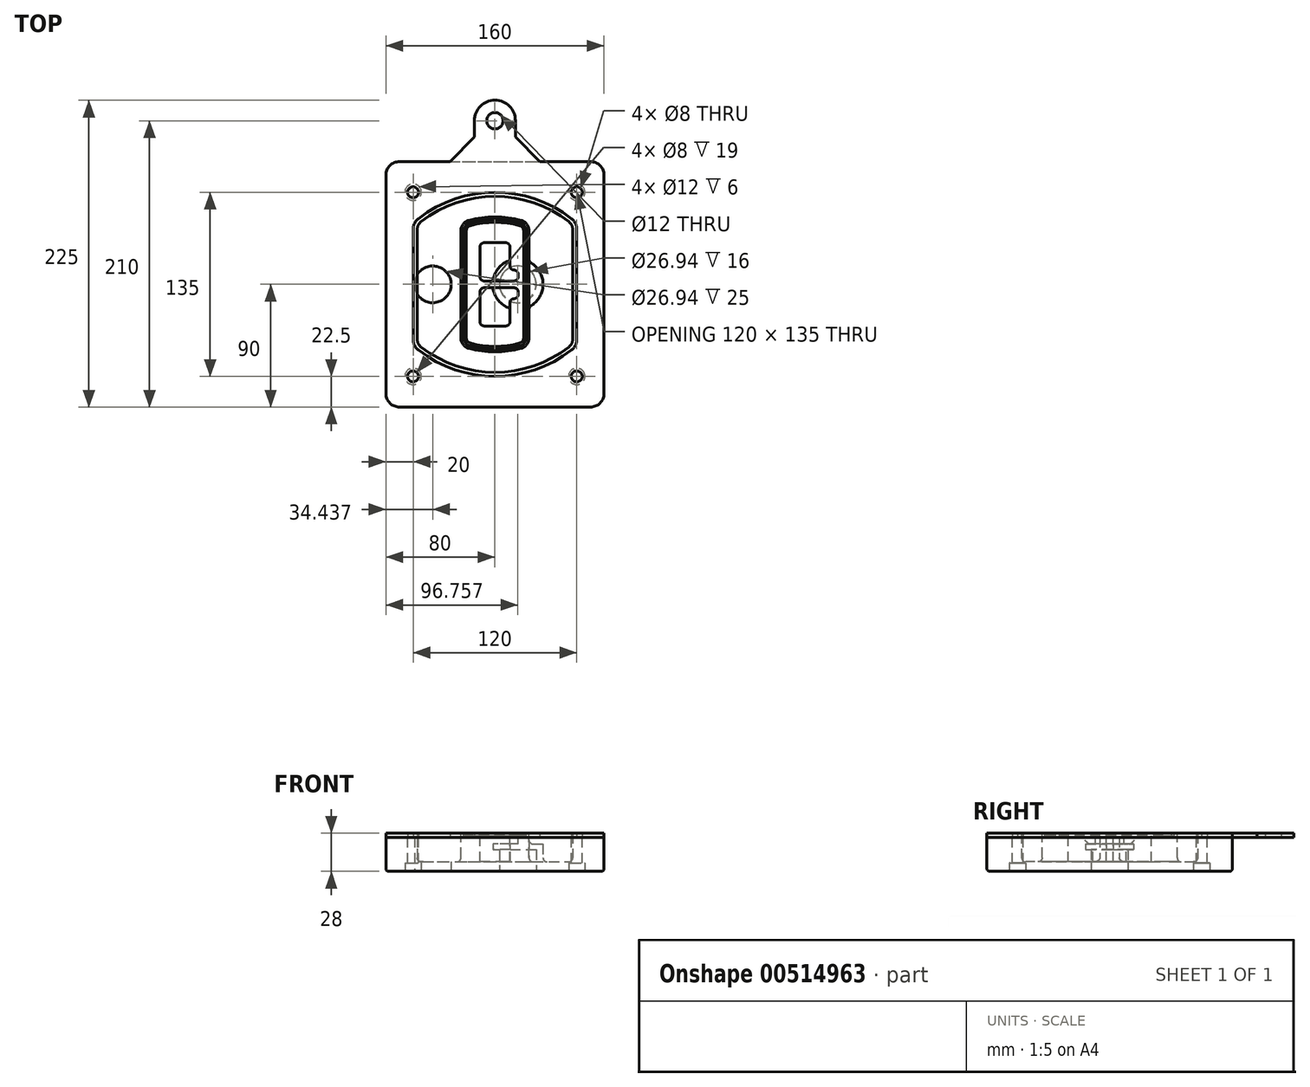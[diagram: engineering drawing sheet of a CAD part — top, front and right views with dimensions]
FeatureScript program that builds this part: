
annotation { "Feature Type Name" : "Feature", "Feature Type Description" : "" }
export const myFeature = defineFeature(function(context is Context, id is Id, definition is map)
    precondition{}
    {
        {
            var Q0;
            Q0=qCreatedBy(makeId("Top.planeOp"),FACE);
            var sketch = newSketch(context, id + "F0", { "sketchPlane" : qUnion([Q0])});
            skPoint(sketch, "E0.rect.middle", {"position": v(0, 0) * mm});
            skLineSegment(sketch, "E1.bottom", {"start": v(-70, -90) * mm, "end": v(70, -90) * mm});
            skLineSegment(sketch, "E1.top", {"start": v(-70, 90) * mm, "end": v(70, 90) * mm});
            skLineSegment(sketch, "E1.left", {"start": v(-80, -80) * mm, "end": v(-80, 80) * mm});
            skLineSegment(sketch, "E1.right", {"start": v(80, -80) * mm, "end": v(80, 80) * mm});
            skLineSegment(sketch, "E2", {"start": v(-80, 90) * mm, "end": v(80, -90) * mm, "construction": true});
            skLineSegment(sketch, "E3", {"start": v(80, 90) * mm, "end": v(-80, -90) * mm, "construction": true});
            skCircle(sketch, "E4", {"center": v(-60, 67.5) * mm, "radius": 4 * mm});
            skCircle(sketch, "E5", {"center": v(60, 67.5) * mm, "radius": 4 * mm});
            skCircle(sketch, "E6", {"center": v(60, -67.5) * mm, "radius": 4 * mm});
            skCircle(sketch, "E7", {"center": v(-60, -67.5) * mm, "radius": 4 * mm});
            skLineSegment(sketch, "E8", {"start": v(-60, 67.5) * mm, "end": v(60, 67.5) * mm, "construction": true});
            skLineSegment(sketch, "E9", {"start": v(60, 67.5) * mm, "end": v(60, -67.5) * mm, "construction": true});
            skLineSegment(sketch, "E10", {"start": v(60, -67.5) * mm, "end": v(-60, -67.5) * mm, "construction": true});
            skLineSegment(sketch, "E11", {"start": v(-60, -67.5) * mm, "end": v(-60, 67.5) * mm, "construction": true});
            skLineSegment(sketch, "E12", {"start": v(-60, 40.3) * mm, "end": v(-60, -40.3) * mm});
            skLineSegment(sketch, "E13", {"start": v(60, 40.3) * mm, "end": v(60, -40.3) * mm});
            skArc(sketch, "E14", {"start": v(56.15, 48.18) * mm, "mid": v(0, 67.5) * mm, "end": v(-56.15, 48.18) * mm});
            skArc(sketch, "E15", {"start": v(-56.15, -48.18) * mm, "mid": v(0, -67.5) * mm, "end": v(56.15, -48.18) * mm});
            skLineSegment(sketch, "E16", {"start": v(-60, 0) * mm, "end": v(60, 0) * mm, "construction": true});
            skPoint(sketch, "E17.visualSharp", {"position": v(-60, -45) * mm});
            skArc(sketch, "E17.filletArc", {"start": v(-60, -40.3) * mm, "mid": v(-58.99, -44.68) * mm, "end": v(-56.15, -48.18) * mm});
            skPoint(sketch, "E18.visualSharp", {"position": v(-60, 45) * mm});
            skArc(sketch, "E18.filletArc", {"start": v(-56.15, 48.18) * mm, "mid": v(-58.99, 44.68) * mm, "end": v(-60, 40.3) * mm});
            skPoint(sketch, "E19.visualSharp", {"position": v(60, 45) * mm});
            skArc(sketch, "E19.filletArc", {"start": v(60, 40.3) * mm, "mid": v(58.99, 44.68) * mm, "end": v(56.15, 48.18) * mm});
            skPoint(sketch, "E20.visualSharp", {"position": v(60, -45) * mm});
            skArc(sketch, "E20.filletArc", {"start": v(56.15, -48.18) * mm, "mid": v(58.99, -44.68) * mm, "end": v(60, -40.3) * mm});
            skPoint(sketch, "E21.visualSharp", {"position": v(-80, 90) * mm});
            skArc(sketch, "E21.filletArc", {"start": v(-70, 90) * mm, "mid": v(-77.07, 87.07) * mm, "end": v(-80, 80) * mm});
            skPoint(sketch, "E22.visualSharp", {"position": v(80, 90) * mm});
            skArc(sketch, "E22.filletArc", {"start": v(80, 80) * mm, "mid": v(77.07, 87.07) * mm, "end": v(70, 90) * mm});
            skPoint(sketch, "E23.visualSharp", {"position": v(80, -90) * mm});
            skArc(sketch, "E23.filletArc", {"start": v(70, -90) * mm, "mid": v(77.07, -87.07) * mm, "end": v(80, -80) * mm});
            skPoint(sketch, "E24.visualSharp", {"position": v(-80, -90) * mm});
            skArc(sketch, "E24.filletArc", {"start": v(-80, -80) * mm, "mid": v(-77.07, -87.07) * mm, "end": v(-70, -90) * mm});
            skArc(sketch, "E25.0", {"start": v(57, 40.3) * mm, "mid": v(56.3, 43.36) * mm, "end": v(54.3, 45.81) * mm});
            skLineSegment(sketch, "E25.1", {"start": v(57, 40.3) * mm, "end": v(57, -40.3) * mm});
            skArc(sketch, "E25.2", {"start": v(54.3, -45.81) * mm, "mid": v(56.3, -43.36) * mm, "end": v(57, -40.3) * mm});
            skArc(sketch, "E25.3", {"start": v(-54.3, -45.81) * mm, "mid": v(0, -64.5) * mm, "end": v(54.3, -45.81) * mm});
            skArc(sketch, "E25.4", {"start": v(-57, -40.3) * mm, "mid": v(-56.3, -43.36) * mm, "end": v(-54.3, -45.81) * mm});
            skArc(sketch, "E25.5", {"start": v(54.3, 45.81) * mm, "mid": v(0, 64.5) * mm, "end": v(-54.3, 45.81) * mm});
            skLineSegment(sketch, "E25.6", {"start": v(-57, 40.3) * mm, "end": v(-57, -40.3) * mm});
            skArc(sketch, "E25.7", {"start": v(-54.3, 45.81) * mm, "mid": v(-56.3, 43.36) * mm, "end": v(-57, 40.3) * mm});
            skArc(sketch, "E26.0", {"start": v(-58.62, 51.33) * mm, "mid": v(-62.58, 46.43) * mm, "end": v(-64, 40.3) * mm});
            skArc(sketch, "E26.1", {"start": v(58.62, 51.33) * mm, "mid": v(0, 71.5) * mm, "end": v(-58.62, 51.33) * mm});
            skArc(sketch, "E26.2", {"start": v(64, 40.3) * mm, "mid": v(62.58, 46.43) * mm, "end": v(58.62, 51.33) * mm});
            skLineSegment(sketch, "E26.3", {"start": v(64, 40.3) * mm, "end": v(64, -40.3) * mm});
            skArc(sketch, "E26.4", {"start": v(58.62, -51.33) * mm, "mid": v(62.58, -46.43) * mm, "end": v(64, -40.3) * mm});
            skLineSegment(sketch, "E26.5", {"start": v(-64, 40.3) * mm, "end": v(-64, -40.3) * mm});
            skArc(sketch, "E26.6", {"start": v(-58.62, -51.33) * mm, "mid": v(0, -71.5) * mm, "end": v(58.62, -51.33) * mm});
            skArc(sketch, "E26.7", {"start": v(-64, -40.3) * mm, "mid": v(-62.58, -46.43) * mm, "end": v(-58.62, -51.33) * mm});
            skSolve(sketch);
        }
        {
            var Q0;
            Q0=makeQuery(id+"F0.imprint","IMPRINT",FACE,{"disambiguationData":[TD([[makeQuery(id+"F0.imprint","IMPRINT",EDGE,{"derivedFrom":sQuery(id+"F0.wireOp",EDGE,"E1.bottom")}),1.0]])]});
            var Q1;
            Q1=makeQuery(id+"F0.imprint","IMPRINT",FACE,{"disambiguationData":[TD([[makeQuery(id+"F0.imprint","IMPRINT",EDGE,{"derivedFrom":sQuery(id+"F0.wireOp",EDGE,"E12")}),1.0]])]});
            var Q2;
            Q2=makeQuery(id+"F0.imprint","IMPRINT",FACE,{"disambiguationData":[TD([[makeQuery(id+"F0.imprint","IMPRINT",EDGE,{"derivedFrom":sQuery(id+"F0.wireOp",EDGE,"E25.0")}),1.0]])]});
            var Q3;
            Q3=makeQuery(id+"F0.imprint","IMPRINT",FACE,{"disambiguationData":[TD([[makeQuery(id+"F0.imprint","IMPRINT",EDGE,{"derivedFrom":sQuery(id+"F0.wireOp",EDGE,"E12")}),-1.0]])]});
            extrude(context, id + "F1", {"entities" : qUnion([Q0, Q1, Q2, Q3]), "oppositeDirection" : true, "depth" : 25 * mm});
        }
        {
            var Q0;
            Q0=makeQuery(id+"F0.imprint","IMPRINT",FACE,{"disambiguationData":[TD([[makeQuery(id+"F0.imprint","IMPRINT",EDGE,{"derivedFrom":sQuery(id+"F0.wireOp",EDGE,"E12")}),1.0]])]});
            extrude(context, id + "F2", {"entities" : qUnion([Q0]), "operationType" : NewBodyOperationType.ADD, "depth" : 3 * mm});
        }
        {
            var Q0;
            Q0=makeQuery(id+"F0.imprint","IMPRINT",FACE,{"disambiguationData":[TD([[makeQuery(id+"F0.imprint","IMPRINT",EDGE,{"derivedFrom":sQuery(id+"F0.wireOp",EDGE,"E25.0")}),1.0]])]});
            extrude(context, id + "F3", {"entities" : qUnion([Q0]), "operationType" : NewBodyOperationType.REMOVE, "oppositeDirection" : true, "depth" : 18 * mm});
        }
        {
            var Q0;
            Q0=makeQuery(id+"F2.opExtrude","CAP_FACE",FACE,{"disambiguationData":[OSD([sQuery(id+"F0.wireOp",EDGE,"E12"),sQuery(id+"F0.wireOp",EDGE,"E13"),sQuery(id+"F0.wireOp",EDGE,"E14"),sQuery(id+"F0.wireOp",EDGE,"E15"),sQuery(id+"F0.wireOp",EDGE,"E17.filletArc"),sQuery(id+"F0.wireOp",EDGE,"E18.filletArc"),sQuery(id+"F0.wireOp",EDGE,"E19.filletArc"),sQuery(id+"F0.wireOp",EDGE,"E20.filletArc"),sQuery(id+"F0.wireOp",EDGE,"E25.0"),sQuery(id+"F0.wireOp",EDGE,"E25.1"),sQuery(id+"F0.wireOp",EDGE,"E25.2"),sQuery(id+"F0.wireOp",EDGE,"E25.3"),sQuery(id+"F0.wireOp",EDGE,"E25.4"),sQuery(id+"F0.wireOp",EDGE,"E25.5"),sQuery(id+"F0.wireOp",EDGE,"E25.6"),sQuery(id+"F0.wireOp",EDGE,"E25.7")])],"isStart":false});
            var sketch = newSketch(context, id + "F4", { "sketchPlane" : qUnion([Q0])});
            skArc(sketch, "E27.0", {"start": v(-19.08, -46.97) * mm, "mid": v(0, -49.5) * mm, "end": v(19.08, -46.97) * mm});
            skArc(sketch, "E28.0", {"start": v(19.08, 46.97) * mm, "mid": v(0, 49.5) * mm, "end": v(-19.08, 46.97) * mm});
            skLineSegment(sketch, "E29", {"start": v(-25, 39.25) * mm, "end": v(-25, -39.25) * mm});
            skLineSegment(sketch, "E30", {"start": v(25, 39.25) * mm, "end": v(25, -39.25) * mm});
            skLineSegment(sketch, "E31", {"start": v(-25, 45.1) * mm, "end": v(25, 45.1) * mm, "construction": true});
            skLineSegment(sketch, "E32", {"start": v(-25, -45.1) * mm, "end": v(25, -45.1) * mm, "construction": true});
            skPoint(sketch, "E33.visualSharp", {"position": v(-25, 45.1) * mm});
            skArc(sketch, "E33.filletArc", {"start": v(-19.08, 46.97) * mm, "mid": v(-23.35, 44.11) * mm, "end": v(-25, 39.25) * mm});
            skPoint(sketch, "E34.visualSharp", {"position": v(25, 45.1) * mm});
            skArc(sketch, "E34.filletArc", {"start": v(25, 39.25) * mm, "mid": v(23.35, 44.11) * mm, "end": v(19.08, 46.97) * mm});
            skPoint(sketch, "E35.visualSharp", {"position": v(25, -45.1) * mm});
            skArc(sketch, "E35.filletArc", {"start": v(19.08, -46.97) * mm, "mid": v(23.35, -44.11) * mm, "end": v(25, -39.25) * mm});
            skPoint(sketch, "E36.visualSharp", {"position": v(-25, -45.1) * mm});
            skArc(sketch, "E36.filletArc", {"start": v(-25, -39.25) * mm, "mid": v(-23.35, -44.11) * mm, "end": v(-19.08, -46.97) * mm});
            skArc(sketch, "E37.0", {"start": v(54.3, 45.81) * mm, "mid": v(0, 64.5) * mm, "end": v(-54.3, 45.81) * mm});
            skArc(sketch, "E37.1", {"start": v(-54.3, 45.81) * mm, "mid": v(-56.3, 43.36) * mm, "end": v(-57, 40.3) * mm});
            skLineSegment(sketch, "E37.2", {"start": v(-57, 40.3) * mm, "end": v(-57, -40.3) * mm});
            skArc(sketch, "E37.3", {"start": v(-57, -40.3) * mm, "mid": v(-56.3, -43.36) * mm, "end": v(-54.3, -45.81) * mm});
            skArc(sketch, "E37.4", {"start": v(-54.3, -45.81) * mm, "mid": v(0, -64.5) * mm, "end": v(54.3, -45.81) * mm});
            skArc(sketch, "E37.5", {"start": v(54.3, -45.81) * mm, "mid": v(56.3, -43.36) * mm, "end": v(57, -40.3) * mm});
            skLineSegment(sketch, "E37.6", {"start": v(57, 40.3) * mm, "end": v(57, -40.3) * mm});
            skArc(sketch, "E37.7", {"start": v(57, 40.3) * mm, "mid": v(56.3, 43.36) * mm, "end": v(54.3, 45.81) * mm});
            skLineSegment(sketch, "E38.0", {"start": v(23, 39.25) * mm, "end": v(23, -39.25) * mm});
            skArc(sketch, "E38.1", {"start": v(18.56, -45.04) * mm, "mid": v(21.76, -42.9) * mm, "end": v(23, -39.25) * mm});
            skArc(sketch, "E38.2", {"start": v(-18.56, -45.04) * mm, "mid": v(0, -47.5) * mm, "end": v(18.56, -45.04) * mm});
            skArc(sketch, "E38.3", {"start": v(-23, -39.25) * mm, "mid": v(-21.76, -42.9) * mm, "end": v(-18.56, -45.04) * mm});
            skLineSegment(sketch, "E38.4", {"start": v(-23, 39.25) * mm, "end": v(-23, -39.25) * mm});
            skArc(sketch, "E38.5", {"start": v(23, 39.25) * mm, "mid": v(21.76, 42.9) * mm, "end": v(18.56, 45.04) * mm});
            skArc(sketch, "E38.6", {"start": v(-18.56, 45.04) * mm, "mid": v(-21.76, 42.9) * mm, "end": v(-23, 39.25) * mm});
            skArc(sketch, "E38.7", {"start": v(18.56, 45.04) * mm, "mid": v(0, 47.5) * mm, "end": v(-18.56, 45.04) * mm});
            skArc(sketch, "E39.0", {"start": v(21, 39.25) * mm, "mid": v(20.18, 41.68) * mm, "end": v(18.04, 43.1) * mm});
            skLineSegment(sketch, "E39.1", {"start": v(21, 39.25) * mm, "end": v(21, -39.25) * mm});
            skArc(sketch, "E39.2", {"start": v(18.04, -43.1) * mm, "mid": v(20.18, -41.68) * mm, "end": v(21, -39.25) * mm});
            skArc(sketch, "E39.3", {"start": v(-18.04, -43.1) * mm, "mid": v(0, -45.5) * mm, "end": v(18.04, -43.1) * mm});
            skArc(sketch, "E39.4", {"start": v(-21, -39.25) * mm, "mid": v(-20.18, -41.68) * mm, "end": v(-18.04, -43.1) * mm});
            skArc(sketch, "E39.5", {"start": v(18.04, 43.1) * mm, "mid": v(0, 45.5) * mm, "end": v(-18.04, 43.1) * mm});
            skLineSegment(sketch, "E39.6", {"start": v(-21, 39.25) * mm, "end": v(-21, -39.25) * mm});
            skArc(sketch, "E39.7", {"start": v(-18.04, 43.1) * mm, "mid": v(-20.18, 41.68) * mm, "end": v(-21, 39.25) * mm});
            skLineSegment(sketch, "E40", {"start": v(-25, 0) * mm, "end": v(25, 0) * mm, "construction": true});
            skLineSegment(sketch, "E41", {"start": v(-11, 5.5) * mm, "end": v(-11, 27.5) * mm});
            skLineSegment(sketch, "E42", {"start": v(-8, 30.5) * mm, "end": v(8, 30.5) * mm});
            skLineSegment(sketch, "E43", {"start": v(11, 27.5) * mm, "end": v(11, 13.5) * mm});
            skLineSegment(sketch, "E44", {"start": v(14, 10.5) * mm, "end": v(14, 10.5) * mm});
            skLineSegment(sketch, "E45", {"start": v(17, 7.5) * mm, "end": v(17, 5.5) * mm});
            skLineSegment(sketch, "E46", {"start": v(14, 2.5) * mm, "end": v(-8, 2.5) * mm});
            skPoint(sketch, "E47.visualSharp", {"position": v(-11, 30.5) * mm});
            skArc(sketch, "E47.filletArc", {"start": v(-8, 30.5) * mm, "mid": v(-10.12, 29.62) * mm, "end": v(-11, 27.5) * mm});
            skPoint(sketch, "E48.visualSharp", {"position": v(11, 30.5) * mm});
            skArc(sketch, "E48.filletArc", {"start": v(11, 27.5) * mm, "mid": v(10.12, 29.62) * mm, "end": v(8, 30.5) * mm});
            skPoint(sketch, "E49.visualSharp", {"position": v(11, 10.5) * mm});
            skArc(sketch, "E49.filletArc", {"start": v(11, 13.5) * mm, "mid": v(11.88, 11.38) * mm, "end": v(14, 10.5) * mm});
            skPoint(sketch, "E50.visualSharp", {"position": v(17, 10.5) * mm});
            skArc(sketch, "E50.filletArc", {"start": v(17, 7.5) * mm, "mid": v(16.12, 9.62) * mm, "end": v(14, 10.5) * mm});
            skPoint(sketch, "E51.visualSharp", {"position": v(17, 2.5) * mm});
            skArc(sketch, "E51.filletArc", {"start": v(14, 2.5) * mm, "mid": v(16.12, 3.38) * mm, "end": v(17, 5.5) * mm});
            skPoint(sketch, "E52.visualSharp", {"position": v(-11, 2.5) * mm});
            skArc(sketch, "E52.filletArc", {"start": v(-11, 5.5) * mm, "mid": v(-10.12, 3.38) * mm, "end": v(-8, 2.5) * mm});
            skLineSegment(sketch, "E53.0.MirrorCS", {"start": v(14, -2.5) * mm, "end": v(-8, -2.5) * mm});
            skArc(sketch, "E54.0.MirrorCS", {"start": v(-11, -5.5) * mm, "mid": v(-10.12, -3.38) * mm, "end": v(-8, -2.5) * mm});
            skLineSegment(sketch, "E55.0.MirrorCS", {"start": v(-11, -5.5) * mm, "end": v(-11, -27.5) * mm});
            skArc(sketch, "E56.0.MirrorCS", {"start": v(-8, -30.5) * mm, "mid": v(-10.12, -29.62) * mm, "end": v(-11, -27.5) * mm});
            skLineSegment(sketch, "E57.0.MirrorCS", {"start": v(-8, -30.5) * mm, "end": v(8, -30.5) * mm});
            skArc(sketch, "E58.0.MirrorCS", {"start": v(11, -27.5) * mm, "mid": v(10.12, -29.62) * mm, "end": v(8, -30.5) * mm});
            skLineSegment(sketch, "E59.0.MirrorCS", {"start": v(11, -27.5) * mm, "end": v(11, -13.5) * mm});
            skArc(sketch, "E60.0.MirrorCS", {"start": v(11, -13.5) * mm, "mid": v(11.88, -11.38) * mm, "end": v(14, -10.5) * mm});
            skArc(sketch, "E61.0.MirrorCS", {"start": v(17, -7.5) * mm, "mid": v(16.12, -9.62) * mm, "end": v(14, -10.5) * mm});
            skLineSegment(sketch, "E62.0.MirrorCS", {"start": v(17, -7.5) * mm, "end": v(17, -5.5) * mm});
            skArc(sketch, "E63.0.MirrorCS", {"start": v(14, -2.5) * mm, "mid": v(16.12, -3.38) * mm, "end": v(17, -5.5) * mm});
            skSolve(sketch);
        }
        {
            var Q0;
            Q0=makeQuery(id+"F4.imprint","IMPRINT",FACE,{"disambiguationData":[TD([[makeQuery(id+"F4.imprint","IMPRINT",EDGE,{"derivedFrom":sQuery(id+"F4.wireOp",EDGE,"E27.0")}),1.0]])]});
            var Q1;
            Q1=makeQuery(id+"F4.imprint","IMPRINT",FACE,{"disambiguationData":[TD([[makeQuery(id+"F4.imprint","IMPRINT",EDGE,{"derivedFrom":sQuery(id+"F4.wireOp",EDGE,"E38.0")}),-1.0]])]});
            var Q2;
            Q2=makeQuery(id+"F4.imprint","IMPRINT",FACE,{"disambiguationData":[TD([[makeQuery(id+"F4.imprint","IMPRINT",EDGE,{"derivedFrom":sQuery(id+"F4.wireOp",EDGE,"E39.0")}),1.0]])]});
            extrude(context, id + "F5", {"entities" : qUnion([Q0, Q1, Q2]), "operationType" : NewBodyOperationType.ADD, "endBound" : BoundingType.UP_TO_NEXT, "oppositeDirection" : true, "depth" : 25 * mm});
        }
        {
            var Q0;
            Q0=makeQuery(id+"F4.imprint","IMPRINT",FACE,{"disambiguationData":[TD([[makeQuery(id+"F4.imprint","IMPRINT",EDGE,{"derivedFrom":sQuery(id+"F4.wireOp",EDGE,"E38.0")}),-1.0]])]});
            extrude(context, id + "F6", {"entities" : qUnion([Q0]), "operationType" : NewBodyOperationType.REMOVE, "oppositeDirection" : true, "depth" : 2 * mm});
        }
        {
            var Q0;
            Q0=makeQuery(id+"F1.opExtrude","CAP_FACE",FACE,{"disambiguationData":[OSD([sQuery(id+"F0.wireOp",EDGE,"E1.bottom"),sQuery(id+"F0.wireOp",EDGE,"E1.top"),sQuery(id+"F0.wireOp",EDGE,"E1.left"),sQuery(id+"F0.wireOp",EDGE,"E1.right"),sQuery(id+"F0.wireOp",EDGE,"E4"),sQuery(id+"F0.wireOp",EDGE,"E5"),sQuery(id+"F0.wireOp",EDGE,"E6"),sQuery(id+"F0.wireOp",EDGE,"E7"),sQuery(id+"F0.wireOp",EDGE,"E21.filletArc"),sQuery(id+"F0.wireOp",EDGE,"E22.filletArc"),sQuery(id+"F0.wireOp",EDGE,"E23.filletArc"),sQuery(id+"F0.wireOp",EDGE,"E24.filletArc")])],"isStart":false});
            var sketch = newSketch(context, id + "F7", { "sketchPlane" : qUnion([Q0])});
            skCircle(sketch, "E64", {"center": v(16.76, 0) * mm, "radius": 13.47 * mm});
            skCircle(sketch, "E65", {"center": v(-45.56, 0) * mm, "radius": 13.47 * mm});
            skLineSegment(sketch, "E66", {"start": v(80, 0) * mm, "end": v(-80, 0) * mm});
            skCircle(sketch, "E67", {"center": v(16.76, 0) * mm, "radius": 18.47 * mm});
            skCircle(sketch, "E68", {"center": v(60, -67.5) * mm, "radius": 6 * mm});
            skCircle(sketch, "E69", {"center": v(-60, -67.5) * mm, "radius": 6 * mm});
            skCircle(sketch, "E70", {"center": v(-60, 67.5) * mm, "radius": 6 * mm});
            skCircle(sketch, "E71", {"center": v(60, 67.5) * mm, "radius": 6 * mm});
            skSolve(sketch);
        }
        {
            var Q0;
            {var subQ1=sQuery(id+"F7.wireOp",EDGE,"E66");var subQ4=sQuery(id+"F7.wireOp",EDGE,"E64");var subQ6=makeQuery(id+"F7.imprint","INTERSECT",VERTEX,{"disambiguationData":[OD(0.0)],"derivedFrom":[subQ4,subQ1]});Q0=makeQuery(id+"F7.imprint","IMPRINT",FACE,{"disambiguationData":[TD([[makeQuery(id+"F7.imprint","IMPRINT",EDGE,{"disambiguationData":[TD([[subQ6,-1.0]])],"derivedFrom":subQ4}),-1.0]])]});}
            var Q1;
            {var subQ0=sQuery(id+"F7.wireOp",EDGE,"E66");var subQ1=sQuery(id+"F7.wireOp",EDGE,"E64");var subQ3=makeQuery(id+"F7.imprint","INTERSECT",VERTEX,{"disambiguationData":[OD(0.0)],"derivedFrom":[subQ1,subQ0]});Q1=makeQuery(id+"F7.imprint","IMPRINT",FACE,{"disambiguationData":[TD([[makeQuery(id+"F7.imprint","IMPRINT",EDGE,{"disambiguationData":[TD([[subQ3,-1.0]])],"derivedFrom":subQ1}),1.0]])]});}
            var Q2;
            {var subQ0=sQuery(id+"F7.wireOp",EDGE,"E66");var subQ1=sQuery(id+"F7.wireOp",EDGE,"E64");var subQ3=makeQuery(id+"F7.imprint","INTERSECT",VERTEX,{"disambiguationData":[OD(0.0)],"derivedFrom":[subQ1,subQ0]});Q2=makeQuery(id+"F7.imprint","IMPRINT",FACE,{"disambiguationData":[TD([[makeQuery(id+"F7.imprint","IMPRINT",EDGE,{"disambiguationData":[TD([[subQ3,1.0]])],"derivedFrom":subQ1}),1.0]])]});}
            var Q3;
            {var subQ1=sQuery(id+"F7.wireOp",EDGE,"E66");var subQ4=sQuery(id+"F7.wireOp",EDGE,"E64");var subQ6=makeQuery(id+"F7.imprint","INTERSECT",VERTEX,{"disambiguationData":[OD(0.0)],"derivedFrom":[subQ4,subQ1]});Q3=makeQuery(id+"F7.imprint","IMPRINT",FACE,{"disambiguationData":[TD([[makeQuery(id+"F7.imprint","IMPRINT",EDGE,{"disambiguationData":[TD([[subQ6,1.0]])],"derivedFrom":subQ4}),-1.0]])]});}
            extrude(context, id + "F8", {"entities" : qUnion([Q0, Q1, Q2, Q3]), "operationType" : NewBodyOperationType.ADD, "oppositeDirection" : true, "depth" : 20 * mm});
        }
        {
            var Q0;
            {var subQ0=sQuery(id+"F7.wireOp",EDGE,"E66");var subQ1=sQuery(id+"F7.wireOp",EDGE,"E64");var subQ3=makeQuery(id+"F7.imprint","INTERSECT",VERTEX,{"disambiguationData":[OD(0.0)],"derivedFrom":[subQ1,subQ0]});Q0=makeQuery(id+"F7.imprint","IMPRINT",FACE,{"disambiguationData":[TD([[makeQuery(id+"F7.imprint","IMPRINT",EDGE,{"disambiguationData":[TD([[subQ3,-1.0]])],"derivedFrom":subQ1}),1.0]])]});}
            var Q1;
            {var subQ0=sQuery(id+"F7.wireOp",EDGE,"E66");var subQ1=sQuery(id+"F7.wireOp",EDGE,"E64");var subQ3=makeQuery(id+"F7.imprint","INTERSECT",VERTEX,{"disambiguationData":[OD(0.0)],"derivedFrom":[subQ1,subQ0]});Q1=makeQuery(id+"F7.imprint","IMPRINT",FACE,{"disambiguationData":[TD([[makeQuery(id+"F7.imprint","IMPRINT",EDGE,{"disambiguationData":[TD([[subQ3,1.0]])],"derivedFrom":subQ1}),1.0]])]});}
            extrude(context, id + "F9", {"entities" : qUnion([Q0, Q1]), "operationType" : NewBodyOperationType.REMOVE, "oppositeDirection" : true, "depth" : 16 * mm});
        }
        {
            var Q0;
            {var subQ0=sQuery(id+"F7.wireOp",EDGE,"E66");var subQ1=sQuery(id+"F7.wireOp",EDGE,"E65");var subQ3=makeQuery(id+"F7.imprint","INTERSECT",VERTEX,{"disambiguationData":[OD(0.0)],"derivedFrom":[subQ1,subQ0]});Q0=makeQuery(id+"F7.imprint","IMPRINT",FACE,{"disambiguationData":[TD([[makeQuery(id+"F7.imprint","IMPRINT",EDGE,{"disambiguationData":[TD([[subQ3,-1.0]])],"derivedFrom":subQ1}),1.0]])]});}
            var Q1;
            {var subQ0=sQuery(id+"F7.wireOp",EDGE,"E66");var subQ1=sQuery(id+"F7.wireOp",EDGE,"E65");var subQ3=makeQuery(id+"F7.imprint","INTERSECT",VERTEX,{"disambiguationData":[OD(0.0)],"derivedFrom":[subQ1,subQ0]});Q1=makeQuery(id+"F7.imprint","IMPRINT",FACE,{"disambiguationData":[TD([[makeQuery(id+"F7.imprint","IMPRINT",EDGE,{"disambiguationData":[TD([[subQ3,1.0]])],"derivedFrom":subQ1}),1.0]])]});}
            extrude(context, id + "F10", {"entities" : qUnion([Q0, Q1]), "operationType" : NewBodyOperationType.REMOVE, "oppositeDirection" : true, "depth" : 25 * mm});
        }
        {
            var Q0;
            Q0=makeQuery(id+"F7.imprint","IMPRINT",FACE,{"disambiguationData":[TD([[makeQuery(id+"F7.imprint","IMPRINT",EDGE,{"derivedFrom":sQuery(id+"F7.wireOp",EDGE,"E68")}),1.0]])]});
            var Q1;
            Q1=makeQuery(id+"F7.imprint","IMPRINT",FACE,{"disambiguationData":[TD([[makeQuery(id+"F7.imprint","IMPRINT",EDGE,{"derivedFrom":makeQuery(id+"F1.opExtrude","CAP_EDGE",EDGE,{"disambiguationData":[OSD([sQuery(id+"F0.wireOp",EDGE,"E5")])],"isStart":false})}),-1.0]])]});
            var Q2;
            Q2=makeQuery(id+"F7.imprint","IMPRINT",FACE,{"disambiguationData":[TD([[makeQuery(id+"F7.imprint","IMPRINT",EDGE,{"derivedFrom":sQuery(id+"F7.wireOp",EDGE,"E69")}),1.0]])]});
            var Q3;
            Q3=makeQuery(id+"F7.imprint","IMPRINT",FACE,{"disambiguationData":[TD([[makeQuery(id+"F7.imprint","IMPRINT",EDGE,{"derivedFrom":makeQuery(id+"F1.opExtrude","CAP_EDGE",EDGE,{"disambiguationData":[OSD([sQuery(id+"F0.wireOp",EDGE,"E4")])],"isStart":false})}),-1.0]])]});
            var Q4;
            Q4=makeQuery(id+"F7.imprint","IMPRINT",FACE,{"disambiguationData":[TD([[makeQuery(id+"F7.imprint","IMPRINT",EDGE,{"derivedFrom":sQuery(id+"F7.wireOp",EDGE,"E70")}),1.0]])]});
            var Q5;
            Q5=makeQuery(id+"F7.imprint","IMPRINT",FACE,{"disambiguationData":[TD([[makeQuery(id+"F7.imprint","IMPRINT",EDGE,{"derivedFrom":makeQuery(id+"F1.opExtrude","CAP_EDGE",EDGE,{"disambiguationData":[OSD([sQuery(id+"F0.wireOp",EDGE,"E7")])],"isStart":false})}),-1.0]])]});
            var Q6;
            Q6=makeQuery(id+"F7.imprint","IMPRINT",FACE,{"disambiguationData":[TD([[makeQuery(id+"F7.imprint","IMPRINT",EDGE,{"derivedFrom":sQuery(id+"F7.wireOp",EDGE,"E71")}),1.0]])]});
            var Q7;
            Q7=makeQuery(id+"F7.imprint","IMPRINT",FACE,{"disambiguationData":[TD([[makeQuery(id+"F7.imprint","IMPRINT",EDGE,{"derivedFrom":makeQuery(id+"F1.opExtrude","CAP_EDGE",EDGE,{"disambiguationData":[OSD([sQuery(id+"F0.wireOp",EDGE,"E6")])],"isStart":false})}),-1.0]])]});
            extrude(context, id + "F11", {"entities" : qUnion([Q0, Q1, Q2, Q3, Q4, Q5, Q6, Q7]), "operationType" : NewBodyOperationType.REMOVE, "oppositeDirection" : true, "depth" : 6 * mm});
        }
        {
            var Q0;
            Q0=makeQuery(id+"F9.boolean.opBoolean","COPY",FACE,{"derivedFrom":makeQuery(id+"F9.opExtrude","CAP_FACE",FACE,{"disambiguationData":[OSD([sQuery(id+"F7.wireOp",EDGE,"E64")])],"isStart":false})});
            var sketch = newSketch(context, id + "F12", { "sketchPlane" : qUnion([Q0])});
            skArc(sketch, "E72.0", {"start": v(11, 17.55) * mm, "mid": v(2.57, 11.82) * mm, "end": v(-1.54, 2.5) * mm});
            skArc(sketch, "E72.1", {"start": v(-1.54, -2.5) * mm, "mid": v(2.57, -11.82) * mm, "end": v(11, -17.55) * mm});
            skLineSegment(sketch, "E73", {"start": v(-1.54, -2.5) * mm, "end": v(14, -2.5) * mm});
            skLineSegment(sketch, "E74.0", {"start": v(14, 2.5) * mm, "end": v(-1.54, 2.5) * mm});
            skArc(sketch, "E74.1", {"start": v(14, 2.5) * mm, "mid": v(16.12, 3.38) * mm, "end": v(17, 5.5) * mm});
            skLineSegment(sketch, "E74.2", {"start": v(17, 7.5) * mm, "end": v(17, 5.5) * mm});
            skArc(sketch, "E74.3", {"start": v(17, 7.5) * mm, "mid": v(16.12, 9.62) * mm, "end": v(14, 10.5) * mm});
            skArc(sketch, "E74.4", {"start": v(11, 13.5) * mm, "mid": v(11.88, 11.38) * mm, "end": v(14, 10.5) * mm});
            skLineSegment(sketch, "E74.5", {"start": v(11, 17.55) * mm, "end": v(11, 13.5) * mm});
            skLineSegment(sketch, "E74.7", {"start": v(14, -2.5) * mm, "end": v(-1.54, -2.5) * mm});
            skArc(sketch, "E74.8", {"start": v(14, -2.5) * mm, "mid": v(16.12, -3.38) * mm, "end": v(17, -5.5) * mm});
            skLineSegment(sketch, "E74.9", {"start": v(17, -7.5) * mm, "end": v(17, -5.5) * mm});
            skArc(sketch, "E74.10", {"start": v(17, -7.5) * mm, "mid": v(16.12, -9.62) * mm, "end": v(14, -10.5) * mm});
            skArc(sketch, "E74.11", {"start": v(11, -13.5) * mm, "mid": v(11.88, -11.38) * mm, "end": v(14, -10.5) * mm});
            skLineSegment(sketch, "E74.12", {"start": v(11, -17.55) * mm, "end": v(11, -13.5) * mm});
            skPoint(sketch, "E75.orphan", {"position": v(11, -27.5) * mm});
            skPoint(sketch, "E76.orphan", {"position": v(-8, -2.5) * mm});
            skPoint(sketch, "E77.orphan", {"position": v(-8, 2.5) * mm});
            skPoint(sketch, "E78.orphan", {"position": v(11, 27.5) * mm});
            skSolve(sketch);
        }
        {
            var Q0;
            {var subQ7=sQuery(id+"F12.wireOp",EDGE,"E72.0");var subQ14=sQuery(id+"F12.wireOp",EDGE,"E72.1");var subQ16=sQuery(id+"F12.wireOp",EDGE,"E74.1");var subQ18=sQuery(id+"F12.wireOp",EDGE,"E74.8");Q0=qUnion([makeQuery(id+"F12.imprint","IMPRINT",FACE,{"disambiguationData":[TD([[makeQuery(id+"F12.imprint","IMPRINT",EDGE,{"derivedFrom":subQ7}),1.0]])]}),makeQuery(id+"F12.imprint","IMPRINT",FACE,{"disambiguationData":[TD([[makeQuery(id+"F12.imprint","IMPRINT",EDGE,{"derivedFrom":subQ14}),1.0]])]}),makeQuery(id+"F12.imprint","IMPRINT",FACE,{"disambiguationData":[TD([[makeQuery(id+"F12.imprint","IMPRINT",EDGE,{"derivedFrom":subQ16}),1.0]])]}),makeQuery(id+"F12.imprint","IMPRINT",FACE,{"disambiguationData":[TD([[makeQuery(id+"F12.imprint","IMPRINT",EDGE,{"derivedFrom":subQ18}),-1.0]])]})]);}
            var Q1;
            Q1=makeQuery(id+"F5.boolean.opBoolean","SPLIT",FACE,{"disambiguationData":[TD([makeQuery(id+"F5.opExtrude","SWEPT_FACE",FACE,{"disambiguationData":[OSD([sQuery(id+"F4.wireOp",EDGE,"E41")])]})])],"derivedFrom":makeQuery(id+"F3.boolean.opBoolean","COPY",FACE,{"derivedFrom":makeQuery(id+"F3.opExtrude","CAP_FACE",FACE,{"disambiguationData":[OSD([sQuery(id+"F0.wireOp",EDGE,"E25.0"),sQuery(id+"F0.wireOp",EDGE,"E25.1"),sQuery(id+"F0.wireOp",EDGE,"E25.2"),sQuery(id+"F0.wireOp",EDGE,"E25.3"),sQuery(id+"F0.wireOp",EDGE,"E25.4"),sQuery(id+"F0.wireOp",EDGE,"E25.5"),sQuery(id+"F0.wireOp",EDGE,"E25.6"),sQuery(id+"F0.wireOp",EDGE,"E25.7")])],"isStart":false})})});
            extrude(context, id + "F13", {"entities" : qUnion([Q0]), "operationType" : NewBodyOperationType.REMOVE, "endBound" : BoundingType.UP_TO_SURFACE, "endBoundEntityFace" : qUnion([Q1]), "depth" : 25 * mm});
        }
        {
            var Q0;
            Q0=makeQuery(id+"F3.boolean.opBoolean","COPY",EDGE,{"derivedFrom":makeQuery(id+"F3.opExtrude","CAP_EDGE",EDGE,{"disambiguationData":[OSD([sQuery(id+"F0.wireOp",EDGE,"E25.6")])],"isStart":false})});
            var Q1;
            Q1=makeQuery(id+"F8.boolean.opBoolean","INTERSECT",EDGE,{"derivedFrom":[makeQuery(id+"F5.opExtrude","SWEPT_FACE",FACE,{"disambiguationData":[OSD([sQuery(id+"F4.wireOp",EDGE,"E30")])]}),makeQuery(id+"F8.opExtrude","CAP_FACE",FACE,{"disambiguationData":[OSD([sQuery(id+"F7.wireOp",EDGE,"E67")])],"isStart":false})]});
            var Q2;
            Q2=makeQuery(id+"F8.boolean.opBoolean","INTERSECT",EDGE,{"disambiguationData":[OD(1.0)],"derivedFrom":[makeQuery(id+"F5.opExtrude","SWEPT_FACE",FACE,{"disambiguationData":[OSD([sQuery(id+"F4.wireOp",EDGE,"E30")])]}),makeQuery(id+"F8.opExtrude","SWEPT_FACE",FACE,{"disambiguationData":[OSD([sQuery(id+"F7.wireOp",EDGE,"E67")])]})]});
            var Q3;
            {var subQ0=sQuery(id+"F4.wireOp",EDGE,"E30");Q3=makeQuery(id+"F8.boolean.opBoolean","SPLIT",EDGE,{"disambiguationData":[TD([makeQuery(id+"F5.opExtrude","SWEPT_FACE",FACE,{"disambiguationData":[OSD([sQuery(id+"F4.wireOp",EDGE,"E35.filletArc")])]})])],"derivedFrom":makeQuery(id+"F5.opExtrude","CAP_EDGE",EDGE,{"disambiguationData":[OSD([subQ0])],"isStart":false})});}
            var Q4;
            {var subQ0=sQuery(id+"F0.wireOp",EDGE,"E25.7");var subQ1=sQuery(id+"F0.wireOp",EDGE,"E25.1");var subQ2=sQuery(id+"F0.wireOp",EDGE,"E25.6");var subQ3=sQuery(id+"F0.wireOp",EDGE,"E25.5");var subQ4=sQuery(id+"F0.wireOp",EDGE,"E25.4");var subQ5=sQuery(id+"F0.wireOp",EDGE,"E25.0");var subQ6=sQuery(id+"F0.wireOp",EDGE,"E25.2");var subQ7=sQuery(id+"F0.wireOp",EDGE,"E25.3");Q4=makeQuery(id+"F8.boolean.opBoolean","INTERSECT",EDGE,{"derivedFrom":[makeQuery(id+"F5.boolean.opBoolean","SPLIT",FACE,{"disambiguationData":[TD([makeQuery(id+"F2.opExtrude","SWEPT_FACE",FACE,{"disambiguationData":[OSD([subQ5])]})])],"derivedFrom":makeQuery(id+"F3.boolean.opBoolean","COPY",FACE,{"derivedFrom":makeQuery(id+"F3.opExtrude","CAP_FACE",FACE,{"disambiguationData":[OSD([subQ5,subQ1,subQ6,subQ7,subQ4,subQ3,subQ2,subQ0])],"isStart":false})})}),makeQuery(id+"F8.opExtrude","SWEPT_FACE",FACE,{"disambiguationData":[OSD([sQuery(id+"F7.wireOp",EDGE,"E67")])]})]});}
            var Q5;
            Q5=makeQuery(id+"F8.boolean.opBoolean","INTERSECT",EDGE,{"disambiguationData":[OD(0.0)],"derivedFrom":[makeQuery(id+"F5.opExtrude","SWEPT_FACE",FACE,{"disambiguationData":[OSD([sQuery(id+"F4.wireOp",EDGE,"E30")])]}),makeQuery(id+"F8.opExtrude","SWEPT_FACE",FACE,{"disambiguationData":[OSD([sQuery(id+"F7.wireOp",EDGE,"E67")])]})]});
            fillet(context, id + "F14", {"entities" : qUnion([Q0, Q1, Q2, Q3, Q4, Q5]), "radius" : 3 * mm, "tangentPropagation" : true, "allowEdgeOverflow" : false});
        }
        {
            var Q0;
            Q0=makeQuery(id+"F1.opExtrude","CAP_EDGE",EDGE,{"disambiguationData":[OSD([sQuery(id+"F0.wireOp",EDGE,"E1.bottom")])],"isStart":false});
            fillet(context, id + "F15", {"entities" : qUnion([Q0]), "radius" : 2 * mm, "tangentPropagation" : true, "allowEdgeOverflow" : false});
        }
        {
            var Q0;
            {var subQ0=sQuery(id+"F0.wireOp",EDGE,"E21.filletArc");var subQ1=sQuery(id+"F0.wireOp",EDGE,"E7");var subQ2=sQuery(id+"F0.wireOp",EDGE,"E6");var subQ3=sQuery(id+"F0.wireOp",EDGE,"E5");var subQ4=sQuery(id+"F0.wireOp",EDGE,"E4");var subQ5=sQuery(id+"F0.wireOp",EDGE,"E22.filletArc");var subQ6=sQuery(id+"F0.wireOp",EDGE,"E1.bottom");var subQ7=sQuery(id+"F0.wireOp",EDGE,"E1.right");var subQ8=sQuery(id+"F0.wireOp",EDGE,"E1.top");var subQ9=sQuery(id+"F0.wireOp",EDGE,"E1.left");var subQ10=sQuery(id+"F0.wireOp",EDGE,"E23.filletArc");var subQ11=sQuery(id+"F0.wireOp",EDGE,"E24.filletArc");Q0=makeQuery(id+"F2.boolean.opBoolean","SPLIT",FACE,{"disambiguationData":[TD([makeQuery(id+"F1.opExtrude","SWEPT_FACE",FACE,{"disambiguationData":[OSD([subQ6])]})])],"derivedFrom":makeQuery(id+"F1.opExtrude","CAP_FACE",FACE,{"disambiguationData":[OSD([subQ6,subQ8,subQ9,subQ7,subQ4,subQ3,subQ2,subQ1,subQ0,subQ5,subQ10,subQ11])],"isStart":true})});}
            var sketch = newSketch(context, id + "F16", { "sketchPlane" : qUnion([Q0])});
            skLineSegment(sketch, "E79", {"start": v(-33, 90) * mm, "end": v(-15, 108) * mm});
            skLineSegment(sketch, "E80", {"start": v(33, 90) * mm, "end": v(15, 108) * mm});
            skLineSegment(sketch, "E81", {"start": v(15, 108) * mm, "end": v(15, 120) * mm});
            skLineSegment(sketch, "E82", {"start": v(-15, 108) * mm, "end": v(-15, 120) * mm});
            skLineSegment(sketch, "E83", {"start": v(0, 90) * mm, "end": v(0, 120) * mm, "construction": true});
            skCircle(sketch, "E84", {"center": v(0, 120) * mm, "radius": 6 * mm});
            skArc(sketch, "E85", {"start": v(15, 120) * mm, "mid": v(0, 135) * mm, "end": v(-15, 120) * mm});
            skLineSegment(sketch, "E86", {"start": v(-80, 0) * mm, "end": v(80, 0) * mm, "construction": true});
            skArc(sketch, "E87.MirrorCS", {"start": v(15, -120) * mm, "mid": v(0, -135) * mm, "end": v(-15, -120) * mm});
            skCircle(sketch, "E88.MirrorC", {"center": v(0, -120) * mm, "radius": 6 * mm});
            skLineSegment(sketch, "E89.MirrorCS", {"start": v(0, -90) * mm, "end": v(0, -120) * mm, "construction": true});
            skLineSegment(sketch, "E90.MirrorCS", {"start": v(-15, -108) * mm, "end": v(-15, -120) * mm});
            skLineSegment(sketch, "E91.MirrorCS", {"start": v(15, -108) * mm, "end": v(15, -120) * mm});
            skLineSegment(sketch, "E92.MirrorCS", {"start": v(33, -90) * mm, "end": v(15, -108) * mm});
            skLineSegment(sketch, "E93.MirrorCS", {"start": v(-33, -90) * mm, "end": v(-15, -108) * mm});
            skSolve(sketch);
        }
        {
            var Q0;
            {var subQ0=sQuery(id+"F16.wireOp",EDGE,"E79");Q0=makeQuery(id+"F16.imprint","IMPRINT",FACE,{"disambiguationData":[TD([[makeQuery(id+"F16.imprint","IMPRINT",EDGE,{"derivedFrom":subQ0}),-1.0]])]});}
            var Q1;
            Q1=makeQuery(id+"F16.imprint","IMPRINT",FACE,{"disambiguationData":[TD([[makeQuery(id+"F16.imprint","IMPRINT",EDGE,{"derivedFrom":sQuery(id+"F16.wireOp",EDGE,"E87.MirrorCS")}),-1.0]])]});
            var Q2;
            Q2=makeQuery(id+"F16.imprint","IMPRINT",FACE,{"disambiguationData":[TD([[makeQuery(id+"F16.imprint","IMPRINT",EDGE,{"derivedFrom":makeQuery(id+"F1.opExtrude","CAP_EDGE",EDGE,{"disambiguationData":[OSD([sQuery(id+"F0.wireOp",EDGE,"E1.left")])],"isStart":true})}),-1.0]])]});
            var Q3;
            Q3=makeQuery(id+"F2.opExtrude","CAP_FACE",FACE,{"disambiguationData":[OSD([sQuery(id+"F0.wireOp",EDGE,"E12"),sQuery(id+"F0.wireOp",EDGE,"E13"),sQuery(id+"F0.wireOp",EDGE,"E14"),sQuery(id+"F0.wireOp",EDGE,"E15"),sQuery(id+"F0.wireOp",EDGE,"E17.filletArc"),sQuery(id+"F0.wireOp",EDGE,"E18.filletArc"),sQuery(id+"F0.wireOp",EDGE,"E19.filletArc"),sQuery(id+"F0.wireOp",EDGE,"E20.filletArc"),sQuery(id+"F0.wireOp",EDGE,"E25.0"),sQuery(id+"F0.wireOp",EDGE,"E25.1"),sQuery(id+"F0.wireOp",EDGE,"E25.2"),sQuery(id+"F0.wireOp",EDGE,"E25.3"),sQuery(id+"F0.wireOp",EDGE,"E25.4"),sQuery(id+"F0.wireOp",EDGE,"E25.5"),sQuery(id+"F0.wireOp",EDGE,"E25.6"),sQuery(id+"F0.wireOp",EDGE,"E25.7")])],"isStart":false});
            extrude(context, id + "F17", {"entities" : qUnion([Q0, Q1, Q2]), "endBound" : BoundingType.UP_TO_SURFACE, "endBoundEntityFace" : qUnion([Q3]), "depth" : 25 * mm});
        }
    });
